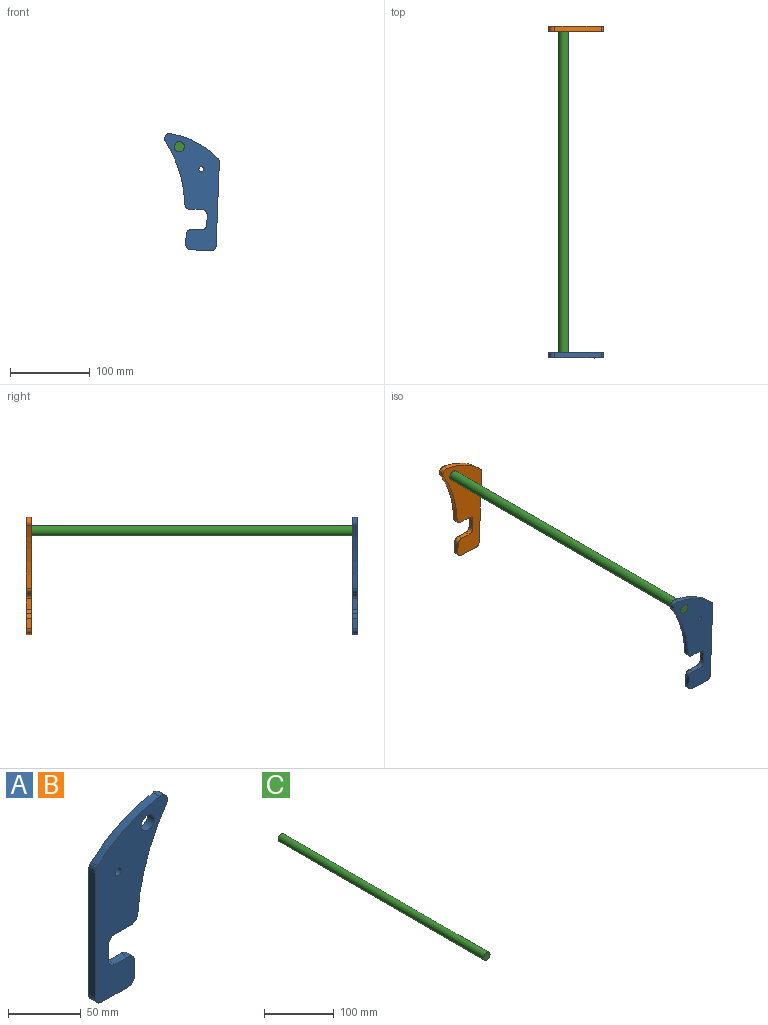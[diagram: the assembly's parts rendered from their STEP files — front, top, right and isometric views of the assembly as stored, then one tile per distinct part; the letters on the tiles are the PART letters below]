
ASSEMBLY  parts=3 mates=2
PART A: 20 faces, bbox 69.7x6.4x144.8 mm
  f0: cylinder r=114.3mm len=60.32mm, axis (0,1,0), area 429.9mm2, adj f9,f10,f12,f14
  f1: plane 105.19x6.35mm, normal (-1,0,0), area 667.9mm2, adj f9,f10,f12,f17
  f2: plane 25.4x6.35mm, normal (0,0,-1), area 161.3mm2, adj f9,f10,f17,f18
  f3: plane 12.7x6.35mm, normal (1,0,0), area 80.6mm2, adj f4,f9,f10,f18
  f4: cylinder r=6.35mm len=6.35mm, axis (0,1,0), area 63.3mm2, adj f3,f5,f9,f10
  f5: plane 12.7x6.35mm, normal (0,0,1), area 80.6mm2, adj f4,f9,f10,f19
  f6: plane 12.7x6.35mm, normal (1,0,0), area 80.6mm2, adj f9,f10,f13,f19
  f7: plane 15.78x6.35mm, normal (0,0,-1), area 100.2mm2, adj f9,f10,f13,f16
  f8: cylinder r=158.75mm len=78.17mm, axis (0,1,0), area 532.1mm2, adj f9,f10,f14,f16
  f9: plane 144.79x69.67mm, normal (0,-1,0), area 5320.1mm2, adj f0,f1,f2,f3,f4,f5,f6,f7
  f10: plane 144.79x69.67mm, normal (0,1,0), area 5320.1mm2, adj f0,f1,f2,f3,f4,f5,f6,f7
  f11: cylinder r=3.17mm len=6.35mm, axis (0,-1,0), area 126.7mm2, adj f9,f10
  f12: cylinder r=6.35mm len=6.35mm, axis (0,1,0), area 33.6mm2, adj f0,f1,f9,f10
  f13: cylinder r=6.35mm len=6.35mm, axis (0,-1,0), area 63.3mm2, adj f6,f7,f9,f10
  f14: cylinder r=6.35mm len=9.94mm, axis (0,-1,0), area 93.4mm2, adj f0,f8,f9,f10
  f15: cylinder r=6.35mm len=12.7mm, axis (0,-1,0), area 253.4mm2, adj f9,f10
  f16: cylinder r=6.35mm len=6.35mm, axis (0,1,0), area 60.4mm2, adj f7,f8,f9,f10
  f17: cylinder r=6.35mm len=6.35mm, axis (0,-1,0), area 63.3mm2, adj f1,f2,f9,f10
  f18: cylinder r=6.35mm len=6.35mm, axis (0,1,0), area 63.3mm2, adj f2,f3,f9,f10
  f19: cylinder r=6.35mm len=6.35mm, axis (0,-1,0), area 63.3mm2, adj f5,f6,f9,f10
PART B: same geometry as A
PART C: 3 faces, bbox 12.7x415.9x12.7 mm
  f0: cylinder r=6.35mm len=415.93mm, axis (0,1,0), area 16594.7mm2, adj f1,f2
  f1: plane 12.7x12.7mm, normal (0,-1,0), area 126.7mm2, adj f0
  f2: plane 12.7x12.7mm, normal (0,1,0), area 126.7mm2, adj f0
PLACE A rot(axis=(-0.02,0,-1),180deg) t=(-94.02,-248.41,-25.21)mm
PLACE B rot(axis=(0.02,0,1),180deg) t=(-94.02,161.16,-25.21)mm
PLACE C rot(axis=(0,1,0),82.9deg) t=(-139.82,167.51,105.24)mm
MATE revolute C.f0 <-> B.f15  axis (0,1,0) through (-139.82,167.51,105.24)mm
MATE planar A.f1 <-> B.f1  axis (1,0,-0.04) through (-91.75,-245.24,33.69)mm
